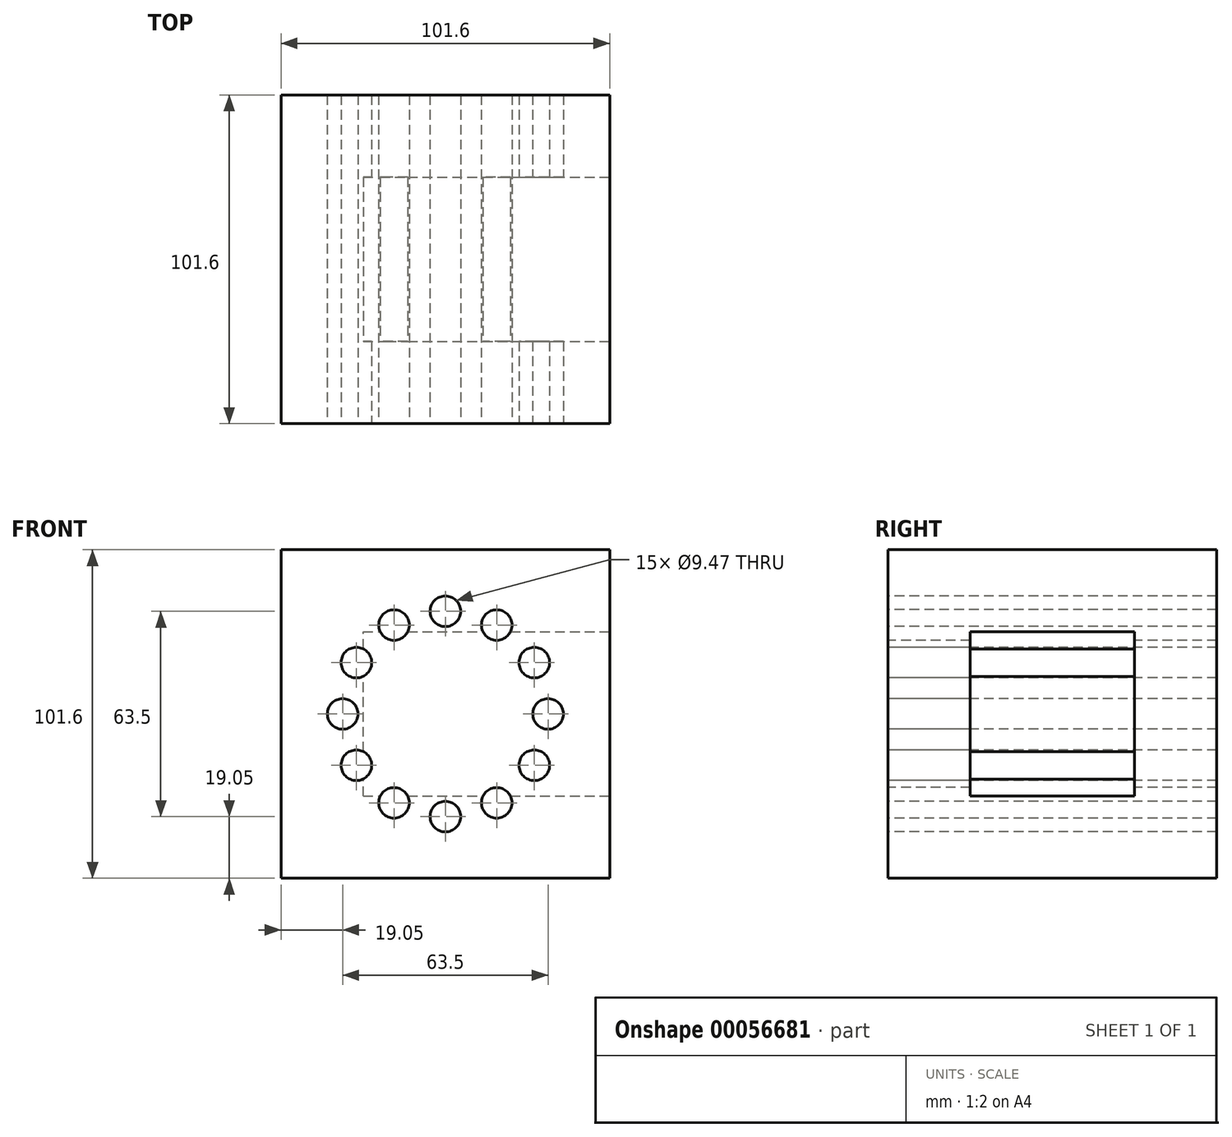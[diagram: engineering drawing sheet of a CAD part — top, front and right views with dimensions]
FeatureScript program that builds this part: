
annotation { "Feature Type Name" : "Feature", "Feature Type Description" : "" }
export const myFeature = defineFeature(function(context is Context, id is Id, definition is map)
    precondition{}
    {
        {
            var Q0;
            Q0=qCreatedBy(makeId("Front.planeOp"),FACE);
            var sketch = newSketch(context, id + "F0", { "sketchPlane" : qUnion([Q0])});
            skLineSegment(sketch, "E0", {"start": v(-50.8, 50.8) * mm, "end": v(-50.8, -50.8) * mm});
            skLineSegment(sketch, "E1", {"start": v(-50.8, -50.8) * mm, "end": v(50.8, -50.8) * mm});
            skLineSegment(sketch, "E2", {"start": v(50.8, -50.8) * mm, "end": v(50.8, 50.8) * mm});
            skLineSegment(sketch, "E3", {"start": v(50.8, 50.8) * mm, "end": v(-50.8, 50.8) * mm});
            skLineSegment(sketch, "E4", {"start": v(-50.8, -50.8) * mm, "end": v(50.8, 50.8) * mm, "construction": true});
            skSolve(sketch);
        }
        {
            var Q0;
            Q0=makeQuery(id+"F0.imprint","IMPRINT",FACE,{"disambiguationData":[TD([[makeQuery(id+"F0.imprint","IMPRINT",EDGE,{"derivedFrom":sQuery(id+"F0.wireOp",EDGE,"E0")}),1.0]])]});
            extrude(context, id + "F1", {"entities" : qUnion([Q0]), "endBound" : BoundingType.SYMMETRIC, "depth" : 101.6 * mm});
        }
        {
            var Q0;
            Q0=makeQuery(id+"F1.opExtrude","CAP_FACE",FACE,{"disambiguationData":[OSD([sQuery(id+"F0.wireOp",EDGE,"E0"),sQuery(id+"F0.wireOp",EDGE,"E1"),sQuery(id+"F0.wireOp",EDGE,"E2"),sQuery(id+"F0.wireOp",EDGE,"E3")])],"isStart":false});
            var sketch = newSketch(context, id + "F2", { "sketchPlane" : qUnion([Q0])});
            skCircle(sketch, "E5", {"center": v(-27.5, 15.88) * mm, "radius": 4.73 * mm});
            skLineSegment(sketch, "E6", {"start": v(-27.5, 15.87) * mm, "end": v(0, 0) * mm, "construction": true});
            skSolve(sketch);
        }
        {
            var Q0;
            Q0=makeQuery(id+"F2.imprint","IMPRINT",FACE,{"disambiguationData":[TD([[makeQuery(id+"F2.imprint","IMPRINT",EDGE,{"derivedFrom":sQuery(id+"F2.wireOp",EDGE,"E5")}),1.0]])]});
            var Q1;
            Q1=sQuery(id+"F2.wireOp",EDGE,"E5");
            extrude(context, id + "F3", {"entities" : qUnion([Q0]), "operationType" : NewBodyOperationType.REMOVE, "surfaceEntities" : qUnion([Q1]), "endBound" : BoundingType.THROUGH_ALL, "oppositeDirection" : true, "depth" : 25.4 * mm});
        }
        {
            var Q0;
            Q0=qCreatedBy(makeId("Top.planeOp"),FACE);
            var sketch = newSketch(context, id + "F4", { "sketchPlane" : qUnion([Q0])});
            skLineSegment(sketch, "E7", {"start": v(0, 53.07) * mm, "end": v(0, -53.07) * mm, "construction": true});
            skSolve(sketch);
        }
        {
            var Q0;
            Q0=makeQuery(id+"F3.boolean.opBoolean","COPY",FACE,{"derivedFrom":makeQuery(id+"F3.opExtrude","SWEPT_FACE",FACE,{"disambiguationData":[OSD([sQuery(id+"F2.wireOp",EDGE,"E5")])]})});
            var Q1;
            Q1=sQuery(id+"F4.wireOp",EDGE,"E7");
            circularPattern(context, id + "F5", {"faces" : qUnion([Q0]), "axis" : qUnion([Q1]), "angle" : 30 * degree, "instanceCount" : 12, "patternType" : PatternType.FACE});
        }
        {
            var Q0;
            Q0=makeQuery(id+"F1.opExtrude","SWEPT_FACE",FACE,{"disambiguationData":[OSD([sQuery(id+"F0.wireOp",EDGE,"E2")])]});
            var sketch = newSketch(context, id + "F6", { "sketchPlane" : qUnion([Q0])});
            skLineSegment(sketch, "E8", {"start": v(25.4, 25.4) * mm, "end": v(-25.4, 25.4) * mm});
            skLineSegment(sketch, "E9", {"start": v(-25.4, 25.4) * mm, "end": v(-25.4, -25.4) * mm});
            skLineSegment(sketch, "E10", {"start": v(-25.4, -25.4) * mm, "end": v(25.4, -25.4) * mm});
            skLineSegment(sketch, "E11", {"start": v(25.4, -25.4) * mm, "end": v(25.4, 25.4) * mm});
            skLineSegment(sketch, "E12", {"start": v(25.4, 25.4) * mm, "end": v(-25.4, -25.4) * mm, "construction": true});
            skSolve(sketch);
        }
        {
            var Q0;
            Q0=makeQuery(id+"F6.imprint","IMPRINT",FACE,{"disambiguationData":[TD([[makeQuery(id+"F6.imprint","IMPRINT",EDGE,{"derivedFrom":sQuery(id+"F6.wireOp",EDGE,"E8")}),1.0]])]});
            extrude(context, id + "F7", {"entities" : qUnion([Q0]), "operationType" : NewBodyOperationType.REMOVE, "oppositeDirection" : true, "depth" : 76.2 * mm});
        }
    });
